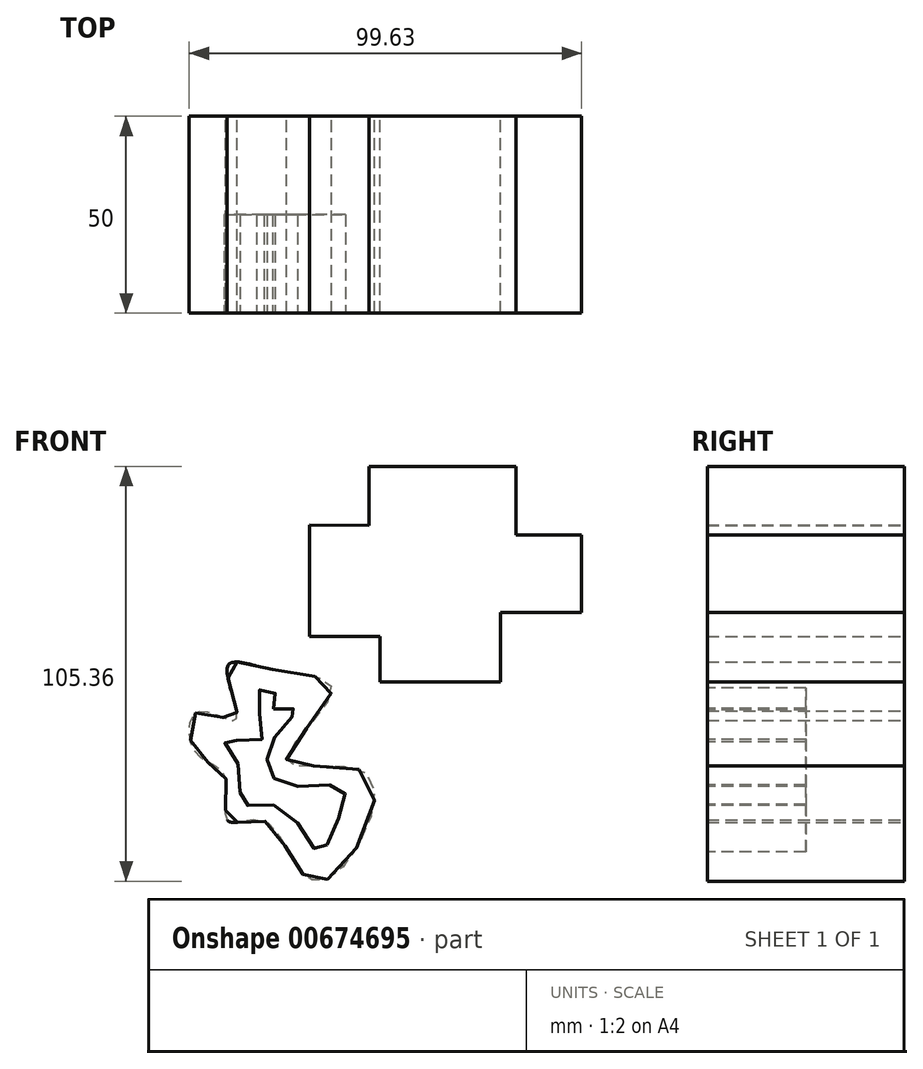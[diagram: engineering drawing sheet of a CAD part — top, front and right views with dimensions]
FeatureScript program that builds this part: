
annotation { "Feature Type Name" : "Feature", "Feature Type Description" : "" }
export const myFeature = defineFeature(function(context is Context, id is Id, definition is map)
    precondition{}
    {
        {
            var Q0;
            Q0=qCreatedBy(makeId("Front.planeOp"),FACE);
            var sketch = newSketch(context, id + "F0", { "sketchPlane" : qUnion([Q0])});
            skLineSegment(sketch, "E0", {"start": v(-41.63, 51.75) * mm, "end": v(-41.63, 23.34) * mm});
            skLineSegment(sketch, "E1", {"start": v(-41.63, 23.34) * mm, "end": v(-23.77, 23.34) * mm});
            skLineSegment(sketch, "E2", {"start": v(-23.77, 23.34) * mm, "end": v(-23.77, 11.78) * mm});
            skLineSegment(sketch, "E3", {"start": v(-23.77, 11.78) * mm, "end": v(6.85, 11.78) * mm});
            skLineSegment(sketch, "E4", {"start": v(6.85, 11.78) * mm, "end": v(6.85, 29.47) * mm});
            skLineSegment(sketch, "E5", {"start": v(6.85, 29.47) * mm, "end": v(27.43, 29.47) * mm});
            skLineSegment(sketch, "E6", {"start": v(27.43, 29.47) * mm, "end": v(27.43, 49.2) * mm});
            skLineSegment(sketch, "E7", {"start": v(27.43, 49.2) * mm, "end": v(10.76, 49.2) * mm});
            skLineSegment(sketch, "E8", {"start": v(10.76, 49.2) * mm, "end": v(10.76, 66.55) * mm});
            skLineSegment(sketch, "E9", {"start": v(10.76, 66.55) * mm, "end": v(-26.5, 66.55) * mm});
            skLineSegment(sketch, "E10", {"start": v(-26.5, 66.55) * mm, "end": v(-26.5, 51.58) * mm});
            skLineSegment(sketch, "E11", {"start": v(-26.5, 51.58) * mm, "end": v(-41.63, 51.75) * mm});
            skFitSpline(sketch, "E12", {"points": [v(-50.98, 15.01) * mm, v(-36.02, 9.57) * mm, v(-47.41, -8.3) * mm, v(-26.83, -11.7) * mm, v(-35.34, -37.2) * mm, v(-44.18, -36.02) * mm, v(-53.36, -23.43) * mm, v(-62.38, -23.43) * mm, v(-63.06, -12.2) * mm, v(-70.71, -5.91) * mm, v(-69.86, 4.3) * mm, v(-60.34, 2.25) * mm, v(-62.55, 15.52) * mm, v(-50.98, 15.01) * mm]});
            skSolve(sketch);
        }
        {
            var Q0;
            Q0=makeQuery(id+"F0.imprint","IMPRINT",FACE,{"disambiguationData":[TD([[makeQuery(id+"F0.imprint","IMPRINT",EDGE,{"derivedFrom":sQuery(id+"F0.wireOp",EDGE,"E0")}),1.0]])]});
            var Q1;
            Q1=makeQuery(id+"F0.imprint","IMPRINT",FACE,{"disambiguationData":[TD([[makeQuery(id+"F0.imprint","IMPRINT",EDGE,{"derivedFrom":sQuery(id+"F0.wireOp",EDGE,"E12")}),-1.0]])]});
            extrude(context, id + "F1", {"entities" : qUnion([Q0, Q1]), "depth" : 50 * mm, "offsetDistance" : 25 * mm});
        }
        {
            var Q0;
            Q0=makeQuery(id+"F1.opExtrude","CAP_FACE",FACE,{"disambiguationData":[OSD([sQuery(id+"F0.wireOp",EDGE,"E0"),sQuery(id+"F0.wireOp",EDGE,"E1"),sQuery(id+"F0.wireOp",EDGE,"E2"),sQuery(id+"F0.wireOp",EDGE,"E3"),sQuery(id+"F0.wireOp",EDGE,"E4"),sQuery(id+"F0.wireOp",EDGE,"E5"),sQuery(id+"F0.wireOp",EDGE,"E6"),sQuery(id+"F0.wireOp",EDGE,"E7"),sQuery(id+"F0.wireOp",EDGE,"E8"),sQuery(id+"F0.wireOp",EDGE,"E9"),sQuery(id+"F0.wireOp",EDGE,"E10"),sQuery(id+"F0.wireOp",EDGE,"E11")])],"isStart":false});
            var sketch = newSketch(context, id + "F2", { "sketchPlane" : qUnion([Q0])});
            skFitSpline(sketch, "E13", {"points": [v(-50.81, 4.98) * mm, v(-50.47, 9.23) * mm, v(-54.9, 9.23) * mm, v(-53.7, -2.68) * mm, v(-63.23, -2.85) * mm, v(-59.83, -8.8) * mm, v(-58.64, -19.18) * mm, v(-48.77, -20.03) * mm, v(-39.42, -31.25) * mm, v(-34.83, -24.1) * mm, v(-33.3, -15.1) * mm, v(-47.24, -14.41) * mm, v(-52.34, -9.14) * mm, v(-48.94, 0) * mm, v(-44.86, 4.98) * mm, v(-50.81, 4.98) * mm]});
            skSolve(sketch);
        }
        {
            var Q0;
            Q0=makeQuery(id+"F2.imprint","IMPRINT",FACE,{"disambiguationData":[TD([[makeQuery(id+"F2.imprint","IMPRINT",EDGE,{"derivedFrom":sQuery(id+"F2.wireOp",EDGE,"E13")}),1.0]])]});
            extrude(context, id + "F3", {"entities" : qUnion([Q0]), "operationType" : NewBodyOperationType.REMOVE, "oppositeDirection" : true, "depth" : 25 * mm, "offsetDistance" : 25 * mm});
        }
    });
